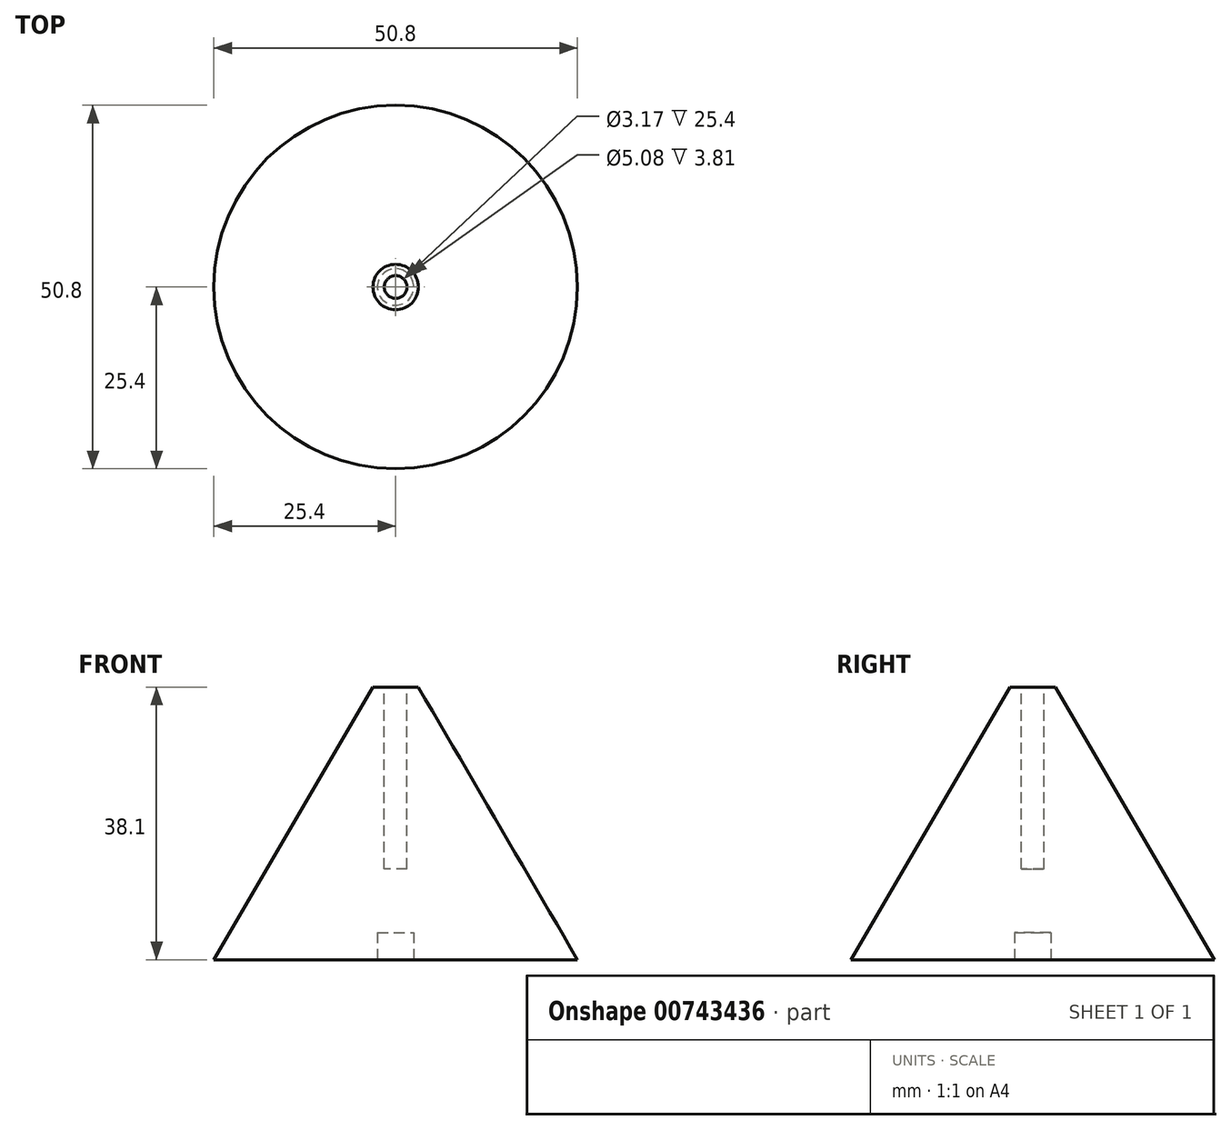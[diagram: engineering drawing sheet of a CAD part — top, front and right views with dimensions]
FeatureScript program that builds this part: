
annotation { "Feature Type Name" : "Feature", "Feature Type Description" : "" }
export const myFeature = defineFeature(function(context is Context, id is Id, definition is map)
    precondition{}
    {
        {
            var Q0;
            Q0=qCreatedBy(makeId("Front.planeOp"),FACE);
            var sketch = newSketch(context, id + "F0", { "sketchPlane" : qUnion([Q0])});
            skLineSegment(sketch, "E0", {"start": v(0, 0) * mm, "end": v(25.4, 0) * mm});
            skLineSegment(sketch, "E1", {"start": v(0, 38.1) * mm, "end": v(0, 0) * mm});
            skLineSegment(sketch, "E2", {"start": v(25.4, 0) * mm, "end": v(3.17, 38.1) * mm});
            skLineSegment(sketch, "E3", {"start": v(3.17, 38.1) * mm, "end": v(0, 38.1) * mm});
            skSolve(sketch);
        }
        {
            var Q0;
            Q0=makeQuery(id+"F0.imprint","IMPRINT",FACE,{"disambiguationData":[TD([[makeQuery(id+"F0.imprint","IMPRINT",EDGE,{"derivedFrom":sQuery(id+"F0.wireOp",EDGE,"E0")}),1.0]])]});
            var Q1;
            Q1=sQuery(id+"F0.wireOp",EDGE,"E1");
            revolve(context, id + "F1", {"surfaceOperationType" : NewSurfaceOperationType.NEW, "entities" : qUnion([Q0]), "axis" : qUnion([Q1]), "revolveType" : RevolveType.FULL});
        }
        {
            var Q0;
            Q0=makeQuery(id+"F1.opRevolve","SWEPT_FACE",FACE,{"disambiguationData":[OSD([sQuery(id+"F0.wireOp",EDGE,"E3")])]});
            var sketch = newSketch(context, id + "F2", { "sketchPlane" : qUnion([Q0])});
            skCircle(sketch, "E4", {"center": v(0, 0) * mm, "radius": 1.59 * mm});
            skSolve(sketch);
        }
        {
            var Q0;
            Q0=makeQuery(id+"F2.imprint","IMPRINT",FACE,{"disambiguationData":[TD([[makeQuery(id+"F2.imprint","IMPRINT",EDGE,{"derivedFrom":sQuery(id+"F2.wireOp",EDGE,"E4")}),1.0]])]});
            extrude(context, id + "F3", {"entities" : qUnion([Q0]), "operationType" : NewBodyOperationType.REMOVE, "oppositeDirection" : true, "depth" : 25.4 * mm, "offsetDistance" : 25.4 * mm});
        }
        {
            var Q0;
            Q0=makeQuery(id+"F1.opRevolve","SWEPT_FACE",FACE,{"disambiguationData":[OSD([sQuery(id+"F0.wireOp",EDGE,"E0")])]});
            var sketch = newSketch(context, id + "F4", { "sketchPlane" : qUnion([Q0])});
            skCircle(sketch, "E5", {"center": v(0, 0) * mm, "radius": 2.54 * mm});
            skSolve(sketch);
        }
        {
            var Q0;
            Q0=makeQuery(id+"F4.imprint","IMPRINT",FACE,{"disambiguationData":[TD([[makeQuery(id+"F4.imprint","IMPRINT",EDGE,{"derivedFrom":sQuery(id+"F4.wireOp",EDGE,"E5")}),1.0]])]});
            extrude(context, id + "F5", {"entities" : qUnion([Q0]), "operationType" : NewBodyOperationType.REMOVE, "oppositeDirection" : true, "depth" : 3.8 * mm, "offsetDistance" : 25.4 * mm});
        }
    });
